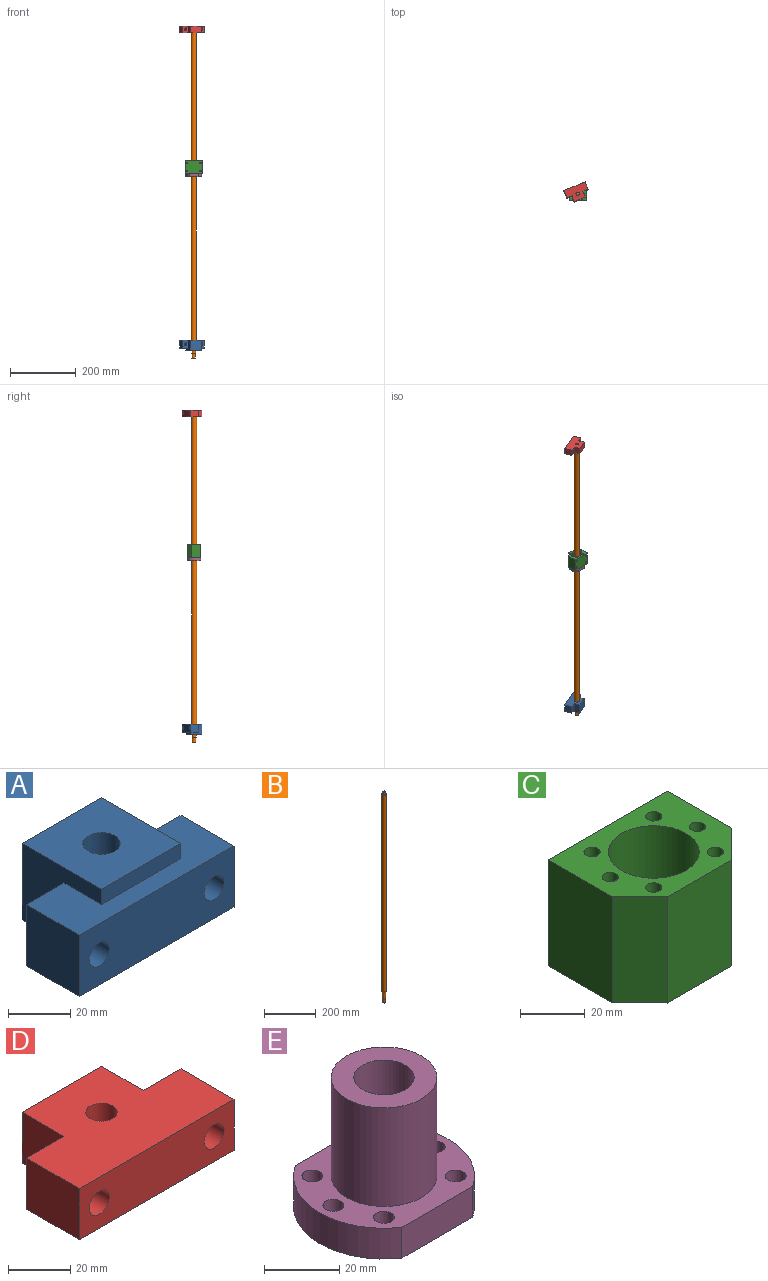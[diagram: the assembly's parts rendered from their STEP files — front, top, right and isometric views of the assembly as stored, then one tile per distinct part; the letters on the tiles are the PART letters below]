
ASSEMBLY  parts=5 mates=9
PART A: 15 faces, bbox 70x43x30 mm
  f0: plane 24x17mm, normal (0,1,0), area 344.4mm2, adj f4,f5,f6,f7,f14
  f1: plane 24x17mm, normal (0,1,0), area 344.4mm2, adj f2,f5,f6,f9,f13
  f2: plane 24x24mm, normal (-1,0,0), area 576mm2, adj f1,f3,f5,f6
  f3: plane 70x24mm, normal (0,-1,0), area 1552.8mm2, adj f2,f4,f5,f6,f13,f14
  f4: plane 24x24mm, normal (1,0,0), area 576mm2, adj f0,f3,f5,f6
  f5: plane 70x24mm, normal (0,0,1), area 1068mm2, adj f0,f1,f2,f3,f4,f7,f9,f10
  f6: plane 70x43mm, normal (0,0,-1), area 2250.9mm2, adj f0,f1,f2,f3,f4,f7,f8,f9
  f7: plane 36x30mm, normal (1,0,0), area 672mm2, adj f0,f5,f6,f8,f10,f12
  f8: plane 36x30mm, normal (0,1,0), area 1080mm2, adj f6,f7,f9,f12
  f9: plane 36x30mm, normal (-1,0,0), area 672mm2, adj f1,f5,f6,f8,f10,f12
  f10: plane 36x6mm, normal (0,-1,0), area 216mm2, adj f5,f7,f9,f12
  f11: cylinder r=6mm len=30mm, axis (0,0,-1), area 1131mm2, adj f6,f12
  f12: plane 36x36mm, normal (0,0,1), area 1182.9mm2, adj f7,f8,f9,f10,f11
  f13: cylinder r=4.5mm len=24mm, axis (0,1,0), area 678.6mm2, adj f1,f3
  f14: cylinder r=4.5mm len=24mm, axis (0,1,0), area 678.6mm2, adj f0,f3
PART B: 9 faces, bbox 16x16x1000 mm
  f0: cylinder r=5mm len=11mm, axis (0,0,-1), area 345.6mm2, adj f1,f2
  f1: plane 10x10mm, normal (0,0,1), area 78.5mm2, adj f0
  f2: plane 16x16mm, normal (0,0,1), area 122.5mm2, adj f0,f4
  f3: plane 16x16mm, normal (0,0,-1), area 88mm2, adj f4,f5
  f4: cylinder r=8mm len=935mm, axis (0,0,-1), area 46998.2mm2, adj f2,f3
  f5: cylinder r=6mm len=39mm, axis (0,0,-1), area 1470.3mm2, adj f3,f6
  f6: plane 12x12mm, normal (0,0,-1), area 34.6mm2, adj f5,f8
  f7: plane 10x10mm, normal (0,0,-1), area 78.5mm2, adj f8
  f8: cylinder r=5mm len=15mm, axis (0,0,-1), area 471.2mm2, adj f6,f7
PART C: 23 faces, bbox 52x40x40 mm
  f0: plane 52x40mm, normal (0,1,0), area 2001.5mm2, adj f1,f11,f13,f14,f15,f17,f19,f21
  f1: plane 40x28mm, normal (-1,0,0), area 1120mm2, adj f0,f2,f13,f14
  f2: plane 40x12mm, normal (-0.71,-0.71,0), area 678.8mm2, adj f1,f3,f13,f14
  f3: plane 40x28mm, normal (0,-1,0), area 1120mm2, adj f2,f4,f13,f14
  f4: plane 40x12mm, normal (0.71,-0.71,0), area 678.8mm2, adj f3,f11,f13,f14
  f5: cylinder r=2.5mm len=40mm, axis (0,0,-1), area 628.3mm2, adj f13,f14
  f6: cylinder r=2.5mm len=40mm, axis (0,0,-1), area 628.3mm2, adj f13,f14
  f7: cylinder r=2.5mm len=40mm, axis (0,0,-1), area 628.3mm2, adj f13,f14
  f8: cylinder r=2.5mm len=40mm, axis (0,0,-1), area 628.3mm2, adj f13,f14
  f9: cylinder r=2.5mm len=40mm, axis (0,0,-1), area 628.3mm2, adj f13,f14
  f10: cylinder r=14mm len=40mm, axis (0,0,-1), area 3518.6mm2, adj f13,f14
  f11: plane 40x28mm, normal (1,0,0), area 1120mm2, adj f0,f4,f13,f14
  f12: cylinder r=2.5mm len=40mm, axis (0,0,-1), area 628.3mm2, adj f13,f14
  f13: plane 52x40mm, normal (0,0,1), area 1202.4mm2, adj f0,f1,f2,f3,f4,f5,f6,f7
  f14: plane 52x40mm, normal (0,0,-1), area 1202.4mm2, adj f0,f1,f2,f3,f4,f5,f6,f7
  f15: cylinder r=2.5mm len=15mm, axis (0,1,0), area 235.6mm2, adj f0,f16
  f16: plane 5x5mm, normal (0,1,0), area 19.6mm2, adj f15
  f17: cylinder r=2.5mm len=15mm, axis (0,1,0), area 235.6mm2, adj f0,f18
  f18: plane 5x5mm, normal (0,1,0), area 19.6mm2, adj f17
  f19: cylinder r=2.5mm len=15mm, axis (0,1,0), area 235.6mm2, adj f0,f20
  f20: plane 5x5mm, normal (0,1,0), area 19.6mm2, adj f19
  f21: cylinder r=2.5mm len=15mm, axis (0,1,0), area 235.6mm2, adj f0,f22
  f22: plane 5x5mm, normal (0,1,0), area 19.6mm2, adj f21
PART D: 13 faces, bbox 70x43x20 mm
  f0: plane 20x17mm, normal (0,1,0), area 276.4mm2, adj f1,f7,f9,f10,f12
  f1: plane 24x20mm, normal (-1,0,0), area 480mm2, adj f0,f2,f9,f10
  f2: plane 70x20mm, normal (0,-1,0), area 1272.8mm2, adj f1,f3,f9,f10,f11,f12
  f3: plane 24x20mm, normal (1,0,0), area 480mm2, adj f2,f4,f9,f10
  f4: plane 20x17mm, normal (0,1,0), area 276.4mm2, adj f3,f5,f9,f10,f11
  f5: plane 20x19mm, normal (1,0,0), area 380mm2, adj f4,f6,f9,f10
  f6: plane 36x20mm, normal (0,1,0), area 720mm2, adj f5,f7,f9,f10
  f7: plane 20x19mm, normal (-1,0,0), area 380mm2, adj f0,f6,f9,f10
  f8: cylinder r=5mm len=20mm, axis (0,0,-1), area 628.3mm2, adj f9,f10
  f9: plane 70x43mm, normal (0,0,1), area 2285.5mm2, adj f0,f1,f2,f3,f4,f5,f6,f7
  f10: plane 70x43mm, normal (0,0,-1), area 2285.5mm2, adj f0,f1,f2,f3,f4,f5,f6,f7
  f11: cylinder r=4.5mm len=24mm, axis (0,1,0), area 678.6mm2, adj f2,f4
  f12: cylinder r=4.5mm len=24mm, axis (0,1,0), area 678.6mm2, adj f0,f2
PART E: 15 faces, bbox 48x40x42 mm
  f0: plane 26.53x10mm, normal (0,1,0), area 265.3mm2, adj f1,f3,f11,f12
  f1: cylinder r=24mm len=40mm, axis (0,0,-1), area 472.9mm2, adj f0,f2,f11,f12
  f2: plane 26.53x10mm, normal (0,-1,0), area 265.3mm2, adj f1,f3,f11,f12
  f3: cylinder r=24mm len=40mm, axis (0,0,-1), area 472.9mm2, adj f0,f2,f11,f12
  f4: cylinder r=2.75mm len=10mm, axis (0,0,-1), area 172.8mm2, adj f11,f12
  f5: cylinder r=2.75mm len=10mm, axis (0,0,-1), area 172.8mm2, adj f11,f12
  f6: cylinder r=2.75mm len=10mm, axis (0,0,-1), area 172.8mm2, adj f11,f12
  f7: cylinder r=2.75mm len=10mm, axis (0,0,-1), area 172.8mm2, adj f11,f12
  f8: cylinder r=2.75mm len=10mm, axis (0,0,-1), area 172.8mm2, adj f11,f12
  f9: cylinder r=2.75mm len=10mm, axis (0,0,-1), area 172.8mm2, adj f11,f12
  f10: cylinder r=8mm len=42mm, axis (0,0,-1), area 2111.2mm2, adj f12,f14
  f11: plane 48x40mm, normal (0,0,1), area 907.2mm2, adj f0,f1,f2,f3,f4,f5,f6,f7
  f12: plane 48x40mm, normal (0,0,-1), area 1321.9mm2, adj f0,f1,f2,f3,f4,f5,f6,f7
  f13: cylinder r=14mm len=32mm, axis (0,0,-1), area 2814.9mm2, adj f11,f14
  f14: plane 28x28mm, normal (0,0,1), area 414.7mm2, adj f10,f13
PLACE A rot(axis=(0.98,0.2,0),180deg) t=(67.94,329.48,986.5)mm
PLACE B t=(0.41,0.08,932.5)mm
PLACE C rot(axis=(1,0,0),180deg) t=(-118.22,56.29,1533)mm
PLACE D rot(axis=(0,0,-1),157.5deg) t=(-249.85,192.49,1921.5)mm
PLACE E t=(-17.19,74.76,1483)mm
MATE planar A.f6 <-> B.f0  axis (0,0,1) through (-51.17,42.1,986.5)mm
MATE planar C.f13 <-> E.f1  axis (0,0,-1) through (-48.45,33.6,1493)mm
MATE cylindrical E.f5 <-> C.f7  axis (0,0,-1) through (-61.88,48.96,1488)mm
MATE cylindrical D.f8 <-> B.f0  axis (0,0,-1) through (-48.45,35.52,1921.5)mm
MATE planar D.f10 <-> B.f0  axis (0,0,-1) through (-51.13,42,1921.5)mm
MATE cylindrical C.f10 <-> E.f1  axis (0,0,1) through (-48.45,35.52,1493)mm
MATE cylindrical E.f1 <-> B.f0  axis (0,0,-1) through (-48.45,35.52,1504)mm
MATE cylindrical E.f9 <-> C.f6  axis (0,0,-1) through (-35.01,48.96,1488)mm
MATE cylindrical A.f11 <-> B.f0  axis (0,0,1) through (-48.45,35.52,986.5)mm
